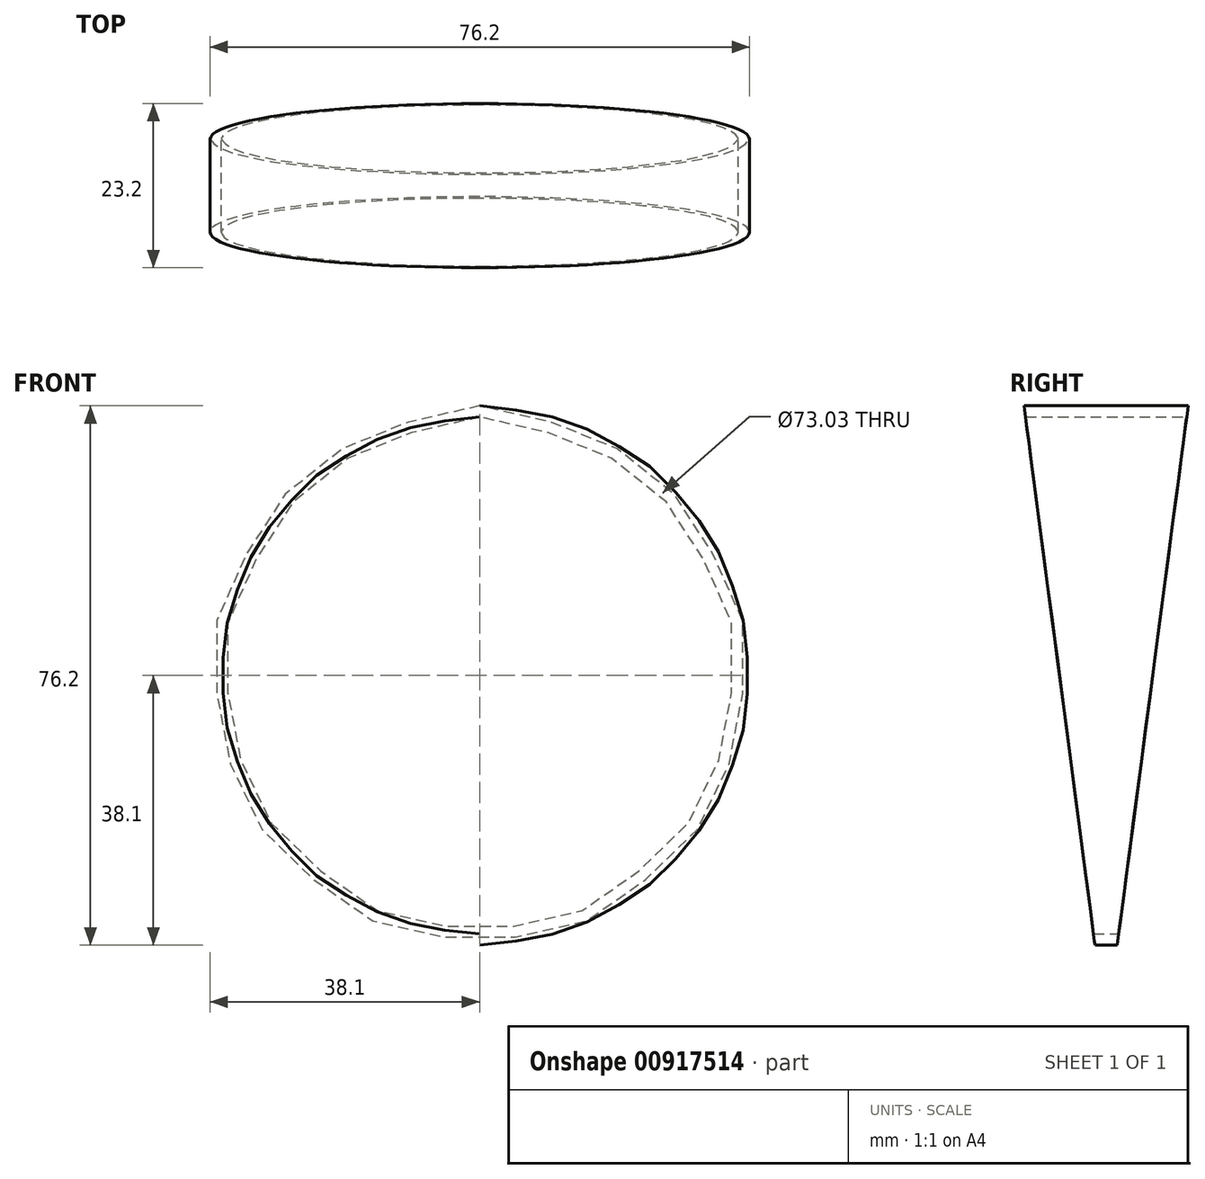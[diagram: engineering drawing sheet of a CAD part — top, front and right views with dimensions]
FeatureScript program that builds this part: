
annotation { "Feature Type Name" : "Feature", "Feature Type Description" : "" }
export const myFeature = defineFeature(function(context is Context, id is Id, definition is map)
    precondition{}
    {
        {
            var Q0;
            Q0=qCreatedBy(makeId("Front.planeOp"),FACE);
            var sketch = newSketch(context, id + "F0", { "sketchPlane" : qUnion([Q0])});
            skCircle(sketch, "E0", {"center": v(0, 38.1) * mm, "radius": 38.1 * mm});
            skCircle(sketch, "E1", {"center": v(0, 38.1) * mm, "radius": 36.51 * mm});
            skPoint(sketch, "E2", {"position": v(0, 0) * mm});
            skSolve(sketch);
        }
        {
            var Q0;
            Q0 = qSketchRegion(id + "F0", true);
            extrude(context, id + "F1", {"entities" : qUnion([Q0]), "endBound" : BoundingType.SYMMETRIC, "depth" : 23.2 * mm, "offsetDistance" : 25.4 * mm});
        }
        {
            var Q0;
            Q0=qCreatedBy(makeId("Right.planeOp"),FACE);
            var sketch = newSketch(context, id + "F2", { "sketchPlane" : qUnion([Q0])});
            skLineSegment(sketch, "E3", {"start": v(-1.56, 0) * mm, "end": v(-11.6, 76.2) * mm});
            skLineSegment(sketch, "E4", {"start": v(-11.6, 76.2) * mm, "end": v(-11.6, -5.5) * mm});
            skLineSegment(sketch, "E5", {"start": v(-11.6, -5.5) * mm, "end": v(11.6, -5.5) * mm});
            skLineSegment(sketch, "E6", {"start": v(11.6, -5.5) * mm, "end": v(11.6, 76.2) * mm});
            skLineSegment(sketch, "E7", {"start": v(11.6, 76.2) * mm, "end": v(1.56, 0) * mm});
            skLineSegment(sketch, "E8", {"start": v(1.56, 0) * mm, "end": v(-1.56, 0) * mm});
            skPoint(sketch, "E9", {"position": v(0, 0) * mm});
            skPoint(sketch, "E10", {"position": v(0, -5.5) * mm});
            skSolve(sketch);
        }
        {
            var Q0;
            Q0 = qSketchRegion(id + "F2", true);
            extrude(context, id + "F3", {"entities" : qUnion([Q0]), "operationType" : NewBodyOperationType.REMOVE, "endBound" : BoundingType.SYMMETRIC, "oppositeDirection" : true, "depth" : 101.6 * mm, "offsetDistance" : 25.4 * mm});
        }
    });
